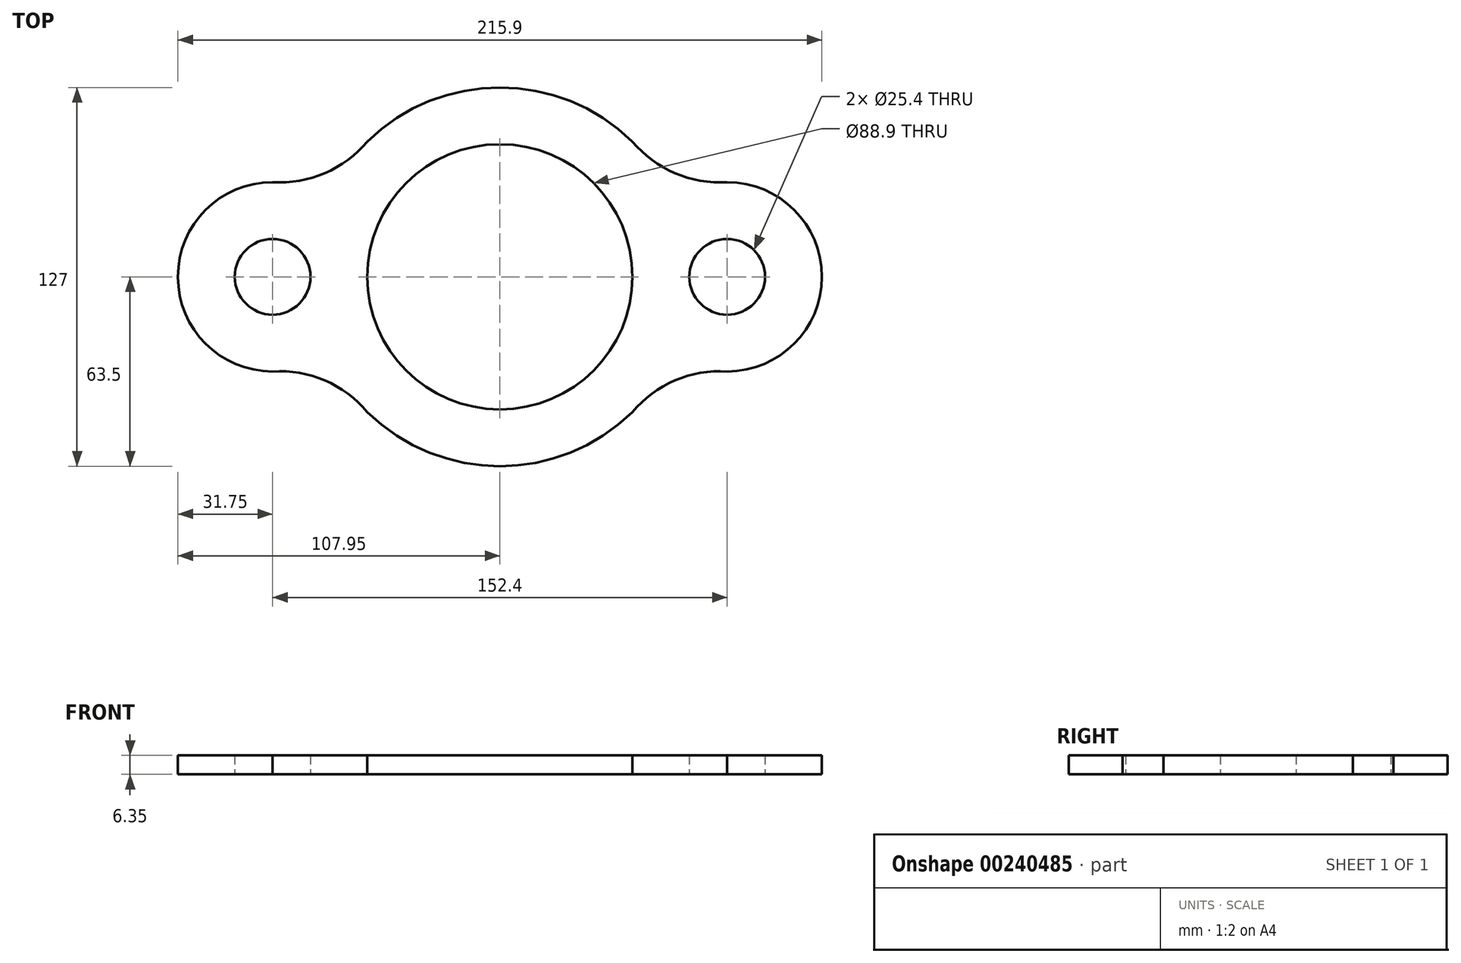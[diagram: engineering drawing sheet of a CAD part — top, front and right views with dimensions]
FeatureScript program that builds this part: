
annotation { "Feature Type Name" : "Feature", "Feature Type Description" : "" }
export const myFeature = defineFeature(function(context is Context, id is Id, definition is map)
    precondition{}
    {
        {
            var Q0;
            Q0=qCreatedBy(makeId("Top.planeOp"),FACE);
            var sketch = newSketch(context, id + "F0", { "sketchPlane" : qUnion([Q0])});
            skCircle(sketch, "E0", {"center": v(-76.2, 0) * mm, "radius": 12.7 * mm});
            skCircle(sketch, "E1", {"center": v(76.2, 0) * mm, "radius": 12.7 * mm});
            skCircle(sketch, "E2", {"center": v(0, 0) * mm, "radius": 44.45 * mm});
            skArc(sketch, "E3", {"start": v(73.92, -31.67) * mm, "mid": v(107.95, 0) * mm, "end": v(73.92, 31.67) * mm});
            skArc(sketch, "E4", {"start": v(-73.92, 31.67) * mm, "mid": v(-107.95, 0) * mm, "end": v(-73.92, -31.67) * mm});
            skArc(sketch, "E5", {"start": v(-47.71, -41.9) * mm, "mid": v(0, -63.5) * mm, "end": v(47.71, -41.9) * mm});
            skArc(sketch, "E6.trimOffspring", {"start": v(47.71, 41.9) * mm, "mid": v(0, 63.5) * mm, "end": v(-47.71, 41.9) * mm});
            skArc(sketch, "E7", {"start": v(44.45, 45.35) * mm, "mid": v(58.7, 34.74) * mm, "end": v(76.2, 31.75) * mm});
            skArc(sketch, "E8", {"start": v(76.2, -31.75) * mm, "mid": v(58.7, -34.74) * mm, "end": v(44.45, -45.35) * mm});
            skArc(sketch, "E9", {"start": v(-76.2, 31.75) * mm, "mid": v(-58.7, 34.74) * mm, "end": v(-44.45, 45.35) * mm});
            skArc(sketch, "E10", {"start": v(-44.45, -45.35) * mm, "mid": v(-58.7, -34.74) * mm, "end": v(-76.2, -31.75) * mm});
            skSolve(sketch);
        }
        {
            var Q0;
            Q0=makeQuery(id+"F0.imprint","IMPRINT",FACE,{"disambiguationData":[TD([[makeQuery(id+"F0.imprint","IMPRINT",EDGE,{"derivedFrom":sQuery(id+"F0.wireOp",EDGE,"E0")}),-1.0]])]});
            extrude(context, id + "F1", {"entities" : qUnion([Q0]), "depth" : 6.35 * mm});
        }
    });
